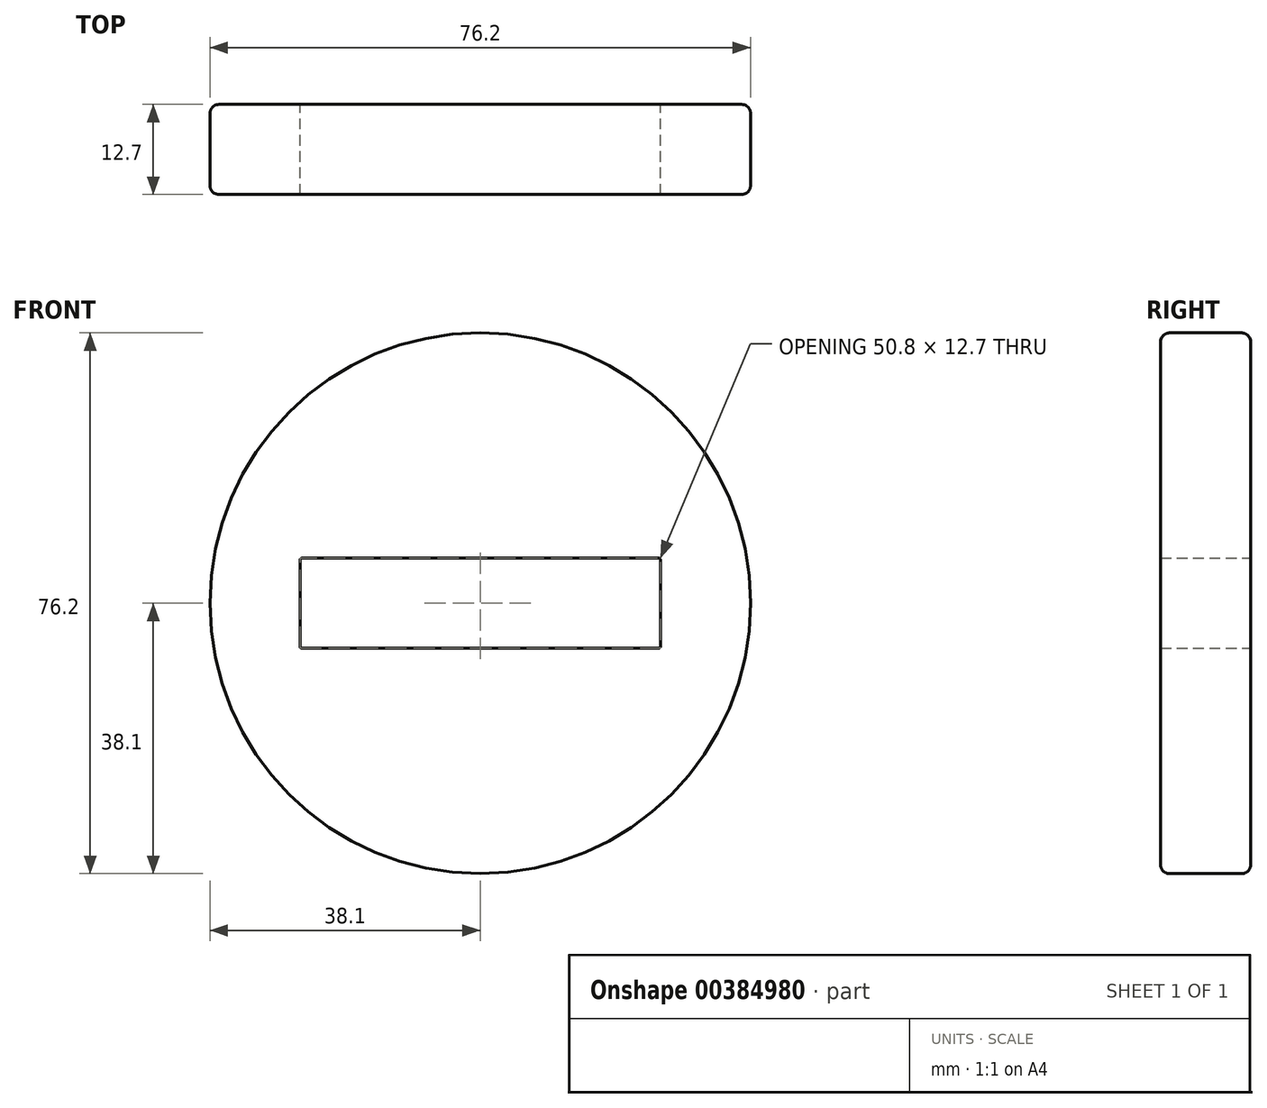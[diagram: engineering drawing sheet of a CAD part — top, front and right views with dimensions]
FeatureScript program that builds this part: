
annotation { "Feature Type Name" : "Feature", "Feature Type Description" : "" }
export const myFeature = defineFeature(function(context is Context, id is Id, definition is map)
    precondition{}
    {
        {
            var Q0;
            Q0=qCreatedBy(makeId("Front.planeOp"),FACE);
            var sketch = newSketch(context, id + "F0", { "sketchPlane" : qUnion([Q0])});
            skCircle(sketch, "E0", {"center": v(0, 0) * mm, "radius": 38.1 * mm});
            skLineSegment(sketch, "E1.bottom", {"start": v(-25.15, 6.35) * mm, "end": v(25.15, 6.35) * mm});
            skLineSegment(sketch, "E1.top", {"start": v(-25.15, -6.35) * mm, "end": v(25.15, -6.35) * mm});
            skLineSegment(sketch, "E1.left", {"start": v(-25.4, 6.1) * mm, "end": v(-25.4, -6.1) * mm});
            skLineSegment(sketch, "E1.right", {"start": v(25.4, 6.1) * mm, "end": v(25.4, -6.1) * mm});
            skLineSegment(sketch, "E2", {"start": v(0, -6.35) * mm, "end": v(0, 6.35) * mm, "construction": true});
            skLineSegment(sketch, "E3", {"start": v(-25.4, 0) * mm, "end": v(25.4, 0) * mm, "construction": true});
            skArc(sketch, "E4.filletArc", {"start": v(-25.15, 6.35) * mm, "mid": v(-25.33, 6.28) * mm, "end": v(-25.4, 6.1) * mm});
            skArc(sketch, "E5.filletArc", {"start": v(25.4, 6.1) * mm, "mid": v(25.33, 6.28) * mm, "end": v(25.15, 6.35) * mm});
            skArc(sketch, "E6.filletArc", {"start": v(25.15, -6.35) * mm, "mid": v(25.33, -6.28) * mm, "end": v(25.4, -6.1) * mm});
            skArc(sketch, "E7.filletArc", {"start": v(-25.4, -6.1) * mm, "mid": v(-25.33, -6.28) * mm, "end": v(-25.15, -6.35) * mm});
            skSolve(sketch);
        }
        {
            var Q0;
            Q0=makeQuery(id+"F0.imprint","IMPRINT",FACE,{"disambiguationData":[TD([[makeQuery(id+"F0.imprint","IMPRINT",EDGE,{"derivedFrom":sQuery(id+"F0.wireOp",EDGE,"E0")}),1.0]])]});
            extrude(context, id + "F1", {"entities" : qUnion([Q0]), "depth" : 12.7 * mm});
        }
        {
            var Q0;
            Q0=makeQuery(id+"F1.opExtrude","CAP_EDGE",EDGE,{"disambiguationData":[OSD([sQuery(id+"F0.wireOp",EDGE,"E0")])],"isStart":false});
            var Q1;
            Q1=makeQuery(id+"F1.opExtrude","CAP_EDGE",EDGE,{"disambiguationData":[OSD([sQuery(id+"F0.wireOp",EDGE,"E0")])],"isStart":true});
            fillet(context, id + "F2", {"entities" : qUnion([Q0, Q1]), "radius" : 1.27 * mm, "tangentPropagation" : true, "allowEdgeOverflow" : false});
        }
    });
